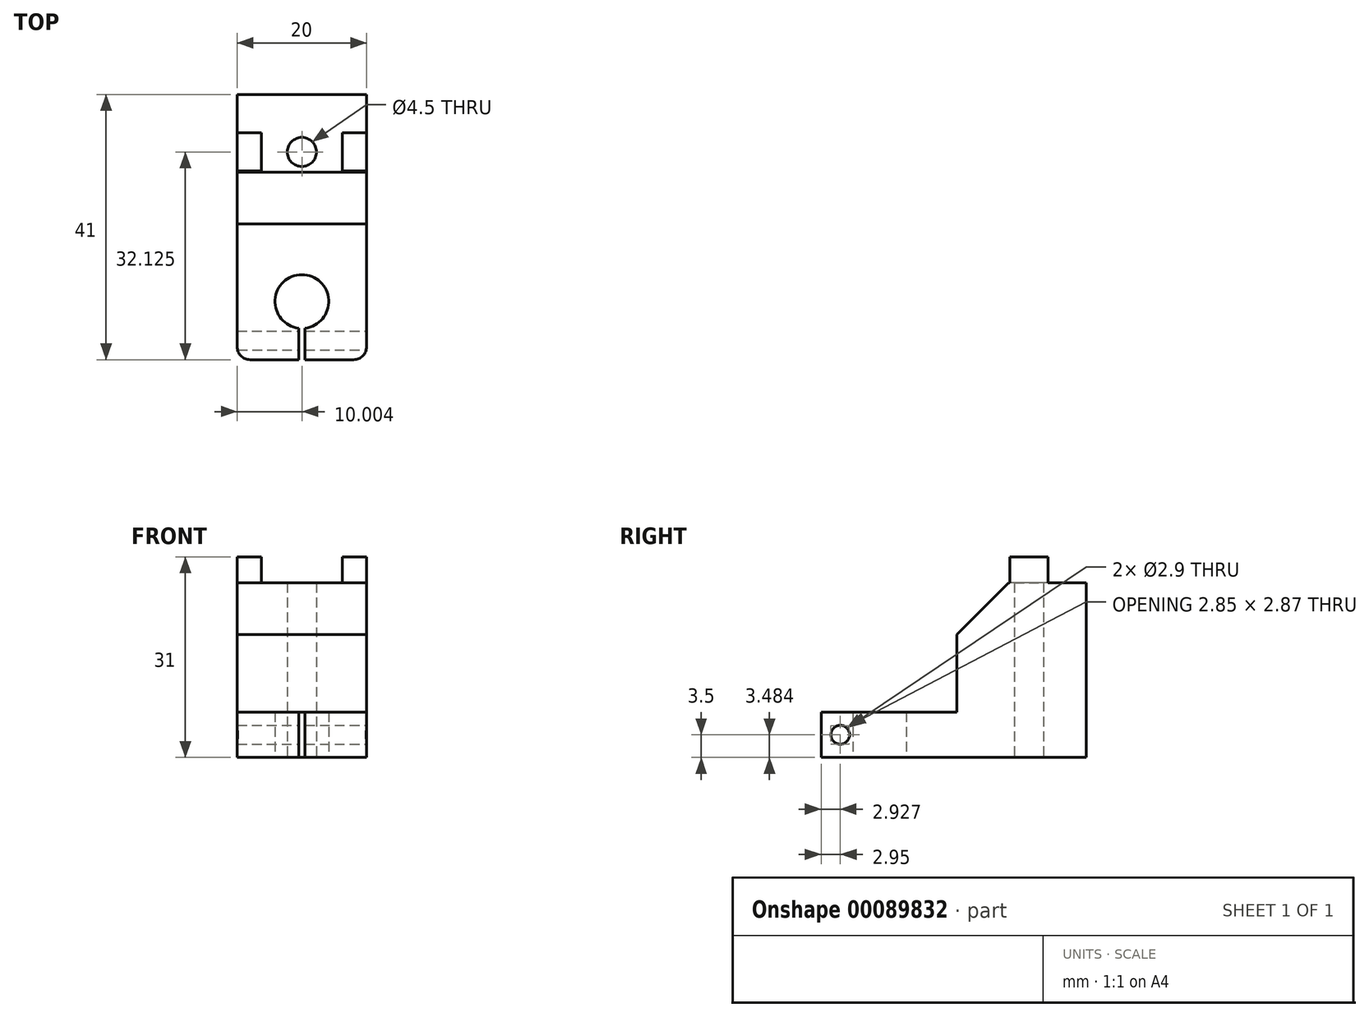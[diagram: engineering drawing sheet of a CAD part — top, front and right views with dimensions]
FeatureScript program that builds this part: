
annotation { "Feature Type Name" : "Feature", "Feature Type Description" : "" }
export const myFeature = defineFeature(function(context is Context, id is Id, definition is map)
    precondition{}
    {
        {
            var Q0;
            Q0=qCreatedBy(makeId("Top.planeOp"),FACE);
            var sketch = newSketch(context, id + "F0", { "sketchPlane" : qUnion([Q0])});
            skLineSegment(sketch, "E0.bottom", {"start": v(-6.6, 0) * mm, "end": v(13.4, 0) * mm});
            skLineSegment(sketch, "E0.top", {"start": v(-6.6, 41) * mm, "end": v(13.4, 41) * mm});
            skLineSegment(sketch, "E0.left", {"start": v(-6.6, 0) * mm, "end": v(-6.6, 41) * mm});
            skLineSegment(sketch, "E0.right", {"start": v(13.4, 0) * mm, "end": v(13.4, 41) * mm});
            skLineSegment(sketch, "E1", {"start": v(-6.6, 21) * mm, "end": v(13.4, 21) * mm, "construction": true});
            skPoint(sketch, "E2.centerSnap0", {"position": v(3.4, 41) * mm});
            skCircle(sketch, "E3", {"center": v(3.4, 9) * mm, "radius": 4.15 * mm});
            skLineSegment(sketch, "E4.bottom", {"start": v(3.9, 0) * mm, "end": v(2.9, 0) * mm});
            skLineSegment(sketch, "E4.top", {"start": v(3.9, 9) * mm, "end": v(2.9, 9) * mm});
            skLineSegment(sketch, "E4.left", {"start": v(3.9, 0) * mm, "end": v(3.9, 9) * mm});
            skLineSegment(sketch, "E4.right", {"start": v(2.9, 0) * mm, "end": v(2.9, 9) * mm});
            skLineSegment(sketch, "E5.bottom", {"start": v(1.15, 32.12) * mm, "end": v(5.65, 32.12) * mm});
            skArc(sketch, "E6", {"start": v(5.65, 32.12) * mm, "mid": v(3.4, 34.38) * mm, "end": v(1.15, 32.12) * mm});
            skLineSegment(sketch, "E7", {"start": v(3.4, 21) * mm, "end": v(3.4, 29.88) * mm});
            skLineSegment(sketch, "E8", {"start": v(3.4, 32.12) * mm, "end": v(3.4, 41) * mm});
            skCircle(sketch, "E9", {"center": v(3.4, 9) * mm, "radius": 7.75 * mm});
            skLineSegment(sketch, "E10", {"start": v(-6.6, 21) * mm, "end": v(13.4, 21) * mm});
            skArc(sketch, "E11", {"start": v(1.15, 32.12) * mm, "mid": v(3.4, 29.88) * mm, "end": v(5.65, 32.12) * mm});
            skLineSegment(sketch, "E12.bottom", {"start": v(-6.6, 35.08) * mm, "end": v(-2.85, 35.08) * mm});
            skLineSegment(sketch, "E12.top", {"start": v(-6.6, 29.18) * mm, "end": v(-2.85, 29.18) * mm});
            skLineSegment(sketch, "E12.left", {"start": v(-6.6, 35.08) * mm, "end": v(-6.6, 29.18) * mm});
            skLineSegment(sketch, "E12.right", {"start": v(-2.85, 35.07) * mm, "end": v(-2.85, 29.17) * mm});
            skLineSegment(sketch, "E13.bottom", {"start": v(13.4, 35.08) * mm, "end": v(9.65, 35.08) * mm});
            skLineSegment(sketch, "E13.top", {"start": v(13.4, 29.18) * mm, "end": v(9.65, 29.18) * mm});
            skLineSegment(sketch, "E13.left", {"start": v(13.4, 35.08) * mm, "end": v(13.4, 29.17) * mm});
            skLineSegment(sketch, "E13.right", {"start": v(9.65, 35.07) * mm, "end": v(9.65, 29.17) * mm});
            skPoint(sketch, "E14", {"position": v(-2.85, 32.12) * mm});
            skSolve(sketch);
        }
        {
            var Q0;
            Q0=makeQuery(id+"F0.imprint","IMPRINT",FACE,{"disambiguationData":[TD([[makeQuery(id+"F0.imprint","IMPRINT",EDGE,{"derivedFrom":sQuery(id+"F0.wireOp",EDGE,"E0.top")}),-1.0]])]});
            var Q1;
            {var subQ1=sQuery(id+"F0.wireOp",EDGE,"E0.bottom");var subQ5=sQuery(id+"F0.wireOp",EDGE,"E0.left");var subQ6=makeQuery(id+"F0.imprint","INTERSECT",VERTEX,{"derivedFrom":[subQ1,subQ5]});Q1=makeQuery(id+"F0.imprint","IMPRINT",FACE,{"disambiguationData":[TD([[makeQuery(id+"F0.imprint","IMPRINT",EDGE,{"disambiguationData":[TD([[subQ6,-1.0]])],"derivedFrom":subQ5}),-1.0]])]});}
            var Q2;
            {var subQ0=sQuery(id+"F0.wireOp",EDGE,"E4.left");var subQ1=sQuery(id+"F0.wireOp",EDGE,"E3");var subQ2=makeQuery(id+"F0.imprint","INTERSECT",VERTEX,{"derivedFrom":[subQ1,subQ0]});Q2=makeQuery(id+"F0.imprint","IMPRINT",FACE,{"disambiguationData":[TD([[makeQuery(id+"F0.imprint","IMPRINT",EDGE,{"disambiguationData":[TD([[subQ2,-1.0]])],"derivedFrom":subQ1}),-1.0]])]});}
            extrude(context, id + "F1", {"entities" : qUnion([Q0, Q1, Q2]), "depth" : 7 * mm});
        }
        {
            var Q0;
            Q0=makeQuery(id+"FQucasgnR9fUPlY_1.boolean.opBoolean","MERGE",FACE,{"derivedFrom":[makeQuery(id+"F1.opExtrude","SWEPT_FACE",FACE,{"disambiguationData":[OSD([sQuery(id+"F0.wireOp",EDGE,"E0.right")])]}),makeQuery(id+"FQucasgnR9fUPlY_1.opExtrude","SWEPT_FACE",FACE,{"disambiguationData":[OSD([sQuery(id+"Fag0aYCVP3Ujfj8_1.wireOp",EDGE,"1siYL01j-m5db-GpVy-yTCy-yeia6Dgr4sKR.left")])]})]});
            var sketch = newSketch(context, id + "F2", { "sketchPlane" : qUnion([Q0])});
            skCircle(sketch, "E15", {"center": v(2.95, 3.5) * mm, "radius": 1.45 * mm});
            skPoint(sketch, "E15.centerSnap0", {"position": v(0, 3.5) * mm});
            skSolve(sketch);
        }
        {
            var Q0;
            Q0=qSketchRegion(id+"F2",true);
            extrude(context, id + "F3", {"entities" : qUnion([Q0]), "operationType" : NewBodyOperationType.REMOVE, "oppositeDirection" : true, "depth" : 25 * mm});
        }
        {
            var Q0;
            Q0=makeQuery(id+"F1.opExtrude","SWEPT_EDGE",EDGE,{"disambiguationData":[OSD([sQuery(id+"F0.wireOp",EDGE,"E0.bottom"),sQuery(id+"F0.wireOp",EDGE,"E0.right")])]});
            var Q1;
            Q1=makeQuery(id+"F1.opExtrude","SWEPT_EDGE",EDGE,{"disambiguationData":[OSD([sQuery(id+"F0.wireOp",EDGE,"E0.bottom"),sQuery(id+"F0.wireOp",EDGE,"E0.left")])]});
            var Q2;
            Q2=makeQuery(id+"F1.opExtrude","SWEPT_EDGE",EDGE,{"disambiguationData":[OSD([sQuery(id+"F0.wireOp",EDGE,"E0.top"),sQuery(id+"F0.wireOp",EDGE,"E0.right")])]});
            var Q3;
            Q3=makeQuery(id+"F1.opExtrude","SWEPT_EDGE",EDGE,{"disambiguationData":[OSD([sQuery(id+"F0.wireOp",EDGE,"E0.top"),sQuery(id+"F0.wireOp",EDGE,"E0.left")])]});
            var Q4;
            Q4=makeQuery(id+"FxEKCNikidz0gRl_1.opExtrude","SWEPT_EDGE",EDGE,{"disambiguationData":[OSD([sQuery(id+"F0.wireOp",EDGE,"E0.left"),sQuery(id+"F0.wireOp",EDGE,"E10")])]});
            var Q5;
            Q5=makeQuery(id+"FxEKCNikidz0gRl_1.opExtrude","SWEPT_EDGE",EDGE,{"disambiguationData":[OSD([sQuery(id+"F0.wireOp",EDGE,"E0.right"),sQuery(id+"F0.wireOp",EDGE,"E10")])]});
            fillet(context, id + "F4", {"entities" : qUnion([Q0, Q1, Q2, Q3, Q4, Q5]), "radius" : 2 * mm, "tangentPropagation" : true, "allowEdgeOverflow" : false});
        }
        {
            var Q0;
            {var subQ0=sQuery(id+"F0.wireOp",EDGE,"E7");Q0=makeQuery(id+"F0.imprint","IMPRINT",FACE,{"disambiguationData":[TD([[makeQuery(id+"F0.imprint","IMPRINT",EDGE,{"derivedFrom":subQ0}),-1.0]])]});}
            var Q1;
            {var subQ0=sQuery(id+"F0.wireOp",EDGE,"E7");Q1=makeQuery(id+"F0.imprint","IMPRINT",FACE,{"disambiguationData":[TD([[makeQuery(id+"F0.imprint","IMPRINT",EDGE,{"derivedFrom":subQ0}),1.0]])]});}
            extrude(context, id + "F5", {"entities" : qUnion([Q0, Q1]), "operationType" : NewBodyOperationType.ADD, "depth" : 27 * mm});
        }
        {
            var Q0;
            Q0=makeQuery(id+"F0.imprint","IMPRINT",FACE,{"disambiguationData":[TD([[makeQuery(id+"F0.imprint","IMPRINT",EDGE,{"derivedFrom":sQuery(id+"F0.wireOp",EDGE,"E12.bottom")}),-1.0]])]});
            var Q1;
            Q1=makeQuery(id+"F0.imprint","IMPRINT",FACE,{"disambiguationData":[TD([[makeQuery(id+"F0.imprint","IMPRINT",EDGE,{"derivedFrom":sQuery(id+"F0.wireOp",EDGE,"E13.bottom")}),1.0]])]});
            extrude(context, id + "F6", {"entities" : qUnion([Q0, Q1]), "operationType" : NewBodyOperationType.ADD, "depth" : 31 * mm});
        }
        {
            var Q0;
            Q0=makeQuery(id+"F5.opExtrude","CAP_EDGE",EDGE,{"disambiguationData":[OSD([sQuery(id+"F0.wireOp",EDGE,"E10")])],"isStart":false});
            chamfer(context, id + "F7", {"entities" : qUnion([Q0]), "width" : 8 * mm, "tangentPropagation" : true});
        }
    });
